# Revit family: QF_ELECTROLUXPROFESSIONAL_1LSNTE_WS6-14_E
name_source: partatom
category: Attrezzature speciali
units: mm (PartAtom-declared; Revit-internal decimal feet)

## family parameters
Basato su piano di lavoro = No
Condiviso = No
Punto di calcolo locali = No
Quota connettore circolare = Usa diametro
Sempre verticale = Sì
Taglio con vuoti quando caricato = No
Tipo di parte = Normale

## types (32) — shared parameters
Depth = 786.6 mm  [stored 2.58071 ft]
Depth Actual = 790 mm  [stored 2.59186 ft]
Height = 1218.8 mm  [stored 3.99869 ft]
Height Actual = 1220 mm  [stored 4.00262 ft]
Latent Heat Output = 0.0
Length Actual = 720 mm  [stored 2.3622 ft]
Modello = WS6-14
Produttore = Electrolux Professional
Sensible Heat Output = 0.0
URL = www.electroluxprofessional.com
Weight = 154
Width = 720 mm  [stored 2.3622 ft]
zero-valued in all types: Gas KW, Prospetto di default, Steam Pounds per Hour

## per-type parameters (varying)
| type | Cycle | Descrizione | Item Number | Phase | Volts | Watts |
| 9867730079 | 50 Hz | WASHER WS6-14 14KG NO HEAT 220-240/50/1N COMPASS PRO 6L01 ML 2xWATER POWDER+5xLIQ. VALV.OPEN SILVER EXT.PM. 2.I/O DISCON | 1LSP3J | 1 | 240 V | 800 W |
| 9867730162 | 60 Hz | WASHER WS6-14 14KG NO HEAT 220-240/60/3 COMPASS PRO 6L01 ML 2xWATER POWDER VALV.OPEN SST DISCON. | 1L999C | 3 | 220 V | 800 W |
| 9867730197 | 50 Hz | WASHER WS6-14 14KG NO HEAT 200/50/60/3 COMPASS PRO 6L41 JP,EN 2xWATER 5xLIQ. VALV.OPEN SST/SILVER 2.I/O DISCON. | 1L0GXN | 3 | 200 V | 900 W |
| 9867730187 | 50 Hz | WASHER WS6-14 14KG NO HEAT 200/50/60/3 COMPASS PRO 6L41 JP,EN 2xWATER POWDER+5xLIQ. VALV.OPEN SILVER 2.I/O DISCON. | 1L827L | 3 | 200 V | 900 W |
| 9867730132 | 50 Hz | WASHER WS6-14 14KG NO HEAT 220-240/50/1N COMPASS PRO 6L01 ML 2xWATER POWDER+5xLIQ. VALV.OPEN SST/SILVER ELS-NETW. EXT.PM | 1L0GDB | 1 | 240 V | 800 W |
| 9867730137 | 50 Hz | WASHER WS6-14 14KG MOP 10KW 380-400/220-230/50/3N/3 COMPASS PRO 6M14 ML 2xWATER POWDER+5xLIQ. EL.VALV.OPEN SILVER 2.I/O | 1L0GFD | 3 | 415 V | 10400 W |
| 9867730033 | 50 Hz | WASHER WS6-14 14KG NO HEAT 200/50/60/3 COMPASS PRO 6L41 JP,EN 2xWATER 5xLIQ. VALV.OPEN SILVER CM. JPY+KRW 2.I/O DISCON. | 1L8230 | 3 | 200 V | 800 W |
| 9867730218 | 50 Hz | WASHER WS6-14 14KG NO HEAT 220-240/50/1N COMPASS PRO 6L01 ML 2xWATER POWDER+5xLIQ. VALV.OPEN SILVER 2.I/O DISCON. | 1L82AF | 1 | 240 V | 800 W |
| 9867730263 | 50 Hz | WASHER WS6-14 14KG EL 10KW 380-415/50/3N COMPASS PRO 6G01 ML 2xWATER POWDER+5xLIQ. VALV.CLOSED SST 2.I/O DISCON. STOP | 1L0HGC | 3 | 415 V | 8800 W |
| 9867730164 | 60 Hz | WASHER WS6-14 14KG NO HEAT 208-240/60/1 COMPASS PRO 6L01 ML 2xWATER POWDER+5xLIQ. VALV.OPEN SILVER ELS-NETW. 2.I/O | 1L0GNB | 1 | 240 V | 800 W |
| 9867730203 | 60 Hz | WASHER WS6-14 14KG EL 10KW 380-415/60/3 COMPASS PRO 6G01 ML 2xWATER POWDER+5xLIQ. VALV.OPEN SILVER 2.I/O TRAFO DISCON. S | 1L0H09 | 3 | 415 V | 10400 W |
| 9867730134 | 60 Hz | WASHER WS6-14 14KG EL 10KW 440/60/3 COMPASS PRO 6G07 ML 2xWATER POWDER+5xLIQ. VALV.OPEN SILVER 2.I/O TRAFO DISCON. STOP | 1L0GEW | 3 | 440 V | 10500 W |
| 9867730114 | 50 Hz | WASHER WS6-14 14KG EL 10KW 380-415/50/3N COMPASS PRO 6A01 SE 2xWATER POWDER VALV.OPEN SILVER DISCON. | 1LA1AC | 3 | 415 V | 10400 W |
| 9867730223 | 50 Hz | WASHER WS6-14 14KG NO HEAT 220-240/50/1N COMPASS PRO 6G01 ML 2xWATER POWDER+5xLIQ. VALV.OPEN SILVER 2.I/O DISCON. STOP | 1LSPSC | 1 | 240 V | 800 W |
| 9867730035 | 50 Hz | WASHER WS6-14 14KG EL 10KW 380-415/50/3N COMPASS PRO 6G01 ML 2xWATER POWDER+5xLIQ. VALV.OPEN SILVER 2.I/O DISCON. STOP | 1L0G8L | 3 | 415 V | 8800 W |
| 9867730161 | 60 Hz | WASHER WS6-14 14KG NO HEAT 220-240/60/3 COMPASS PRO 6L01 ML 2xWATER POWDER VALV.OPEN SILVER DISCON. | 1L0GLK | 3 | 220 V | 800 W |
| 9867730121 | 60 Hz | WASHER WS6-14 14KG NO HEAT 115/60/1N COMPASS PRO 6G01 ML 2xWATER POWDER VALV.OPEN SILVER TRAFO DISCON. STOP | 1LA1BL | 1 | 115 V | 800 W |
| 9867730080 | 50 Hz | WASHER WS6-14 14KG EL 10KW 380-415/220-240/50/3N/3 COMPASS PRO 6G01 ML 2xWATER POWDER+5xLIQ. VALV.OPEN SILVER 2.I/O DISC | 1LSP5K | 3 | 415 V | 10400 W |
| 9867730149 | 50 Hz | WASHER WS6-14 14KG EL 10KW 380-415/50/3N COMPASS PRO 6H01 ML 2xWATER POWDER+5xLIQ. EL.VALV.OPEN SILVER 2.I/O QC DISCON. | 1L0GHP | 3 | 415 V | 10400 W |
| 9867730241 | 60 Hz | WASHER WS6-14 14KG EL 10KW 480/60/3 COMPASS PRO 6G01 ML 2xWATER POWDER+5xLIQ. VALV.OPEN SILVER 2.I/O TRAFO DISCON. STOP | 1L0H8K | 3 | 480 V | 10500 W |
| 9867730156 | 50 Hz | WASHER WS6-14 14KG MOP 10KW 380-415/50/3N COMPASS PRO 6M14 SE 2xWATER POWDER+ED EL.VALV.OPEN SILVER QC DISCON. STOP LID | 1LA21Y | 3 | 415 V | 10400 W |
| 9867730116 | 50 Hz | WASHER WS6-14 14KG NO HEAT 200/50/60/3 COMPASS PRO 6L41 JP,EN 2xWATER 5xLIQ. VALV.OPEN SILVER 2.I/O DISCON. | 1LA1AW | 3 | 200 V | 900 W |
| 9867730249 | 50 Hz | WASHER WS6-14 14KG EL 10KW 380-415/50/3N COMPASS PRO 6G01 ML 2xWATER POWDER+5xLIQ. VALV.CLOSED SILVER 2.I/O DISCON. STOP | 1LM0AS | 3 | 415 V | 8800 W |
| 9867730068 | 50 Hz | WASHER WS6-14 14KG MOP 10KW 380-415/50/3N COMPASS PRO 6F01 ML 2xWATER POWDER+ED EL.VALV.OPEN SST DISCON. STOP LID | 1LSP5F | 3 | 415 V | 8800 W |
| 9867730078 | 50 Hz | WASHER WS6-14 14KG NO HEAT 220-240/50/1N COMPASS PRO 6L01 ML 2xWATER POWDER VALV.OPEN SILVER EXT.PM. 2.I/O DISCON. | 1LSP5J | 1 | 240 V | 800 W |
| 9867730219 | 60 Hz | WASHER WS6-14 14KG EL 10KW 208-240/60/3 COMPASS PRO 6G01 ML 2xWATER POWDER+5xLIQ. VALV.CLOSED SILVER 2.I/O DISCON. STOP | 1L0H1T | 3 | 240 V | 10400 W |
| 9867730173 | 50 Hz | WASHER WS6-14 14KG NO HEAT 220-240/50/1N COMPASS PRO 6G01 CH-EN 2xWATER POWDER VALV.OPEN SILVER DISCON. STOP | 1L0GSZ | 1 | 240 V | 800 W |
| 9867730042 | 50 Hz | WASHER WS6-14 14KG MOP 10KW 380-400/50/3N COMPASS PRO 6M14 ML 2xWATER POWDER+ED EL.VALV.OPEN SST DISCON. STOP LID | 1LSNWW | 3 | 400 V | 10400 W |
| 9867730130 | 60 Hz | WASHER WS6-14 14KG NO HEAT 208-240/60/1 COMPASS PRO 6G01 ML 2xWATER POWDER+5xLIQ. VALV.CLOSED SILVER 2.I/O STOP | 1LSPAN | 1 | 240 V | 800 W |
| 9867730158 | 60 Hz | WASHER WS6-14 14KG EL 7,5KW 440/60/3 COMPASS PRO 6G07 ML 2xWATER POWDER+5xLIQ. EL.VALV.OPEN SILVER 2.I/O TRAFO DISCON. S | 1L0GKL | 3 | 440 V | 10500 W |
| 9867730099 | 50 Hz | WASHER WS6-14 14KG EL 10KW 380-415/50/3N COMPASS PRO 6G01 ML 2xWATER POWDER+5xLIQ. VALV.OPEN SST/SILVER 2.I/O DISCON. ST | 1L821L | 3 | 415 V | 10400 W |
| 9867730128 | 50 Hz | WASHER WS6-14 14KG EL 10KW 380-415/50/3N COMPASS PRO 6G01 CH-EN 2xWATER POWDER VALV.OPEN SILVER DISCON. STOP | 1LSPA2 | 3 | 415 V | 10400 W |

note: [stored X ft] marks values corroborated as IEEE doubles in the binary element streams (Revit-internal decimal feet)

## geometry (parser evidence)
native form markers: Sweep x4
no freeform markers — native parametric forms only
